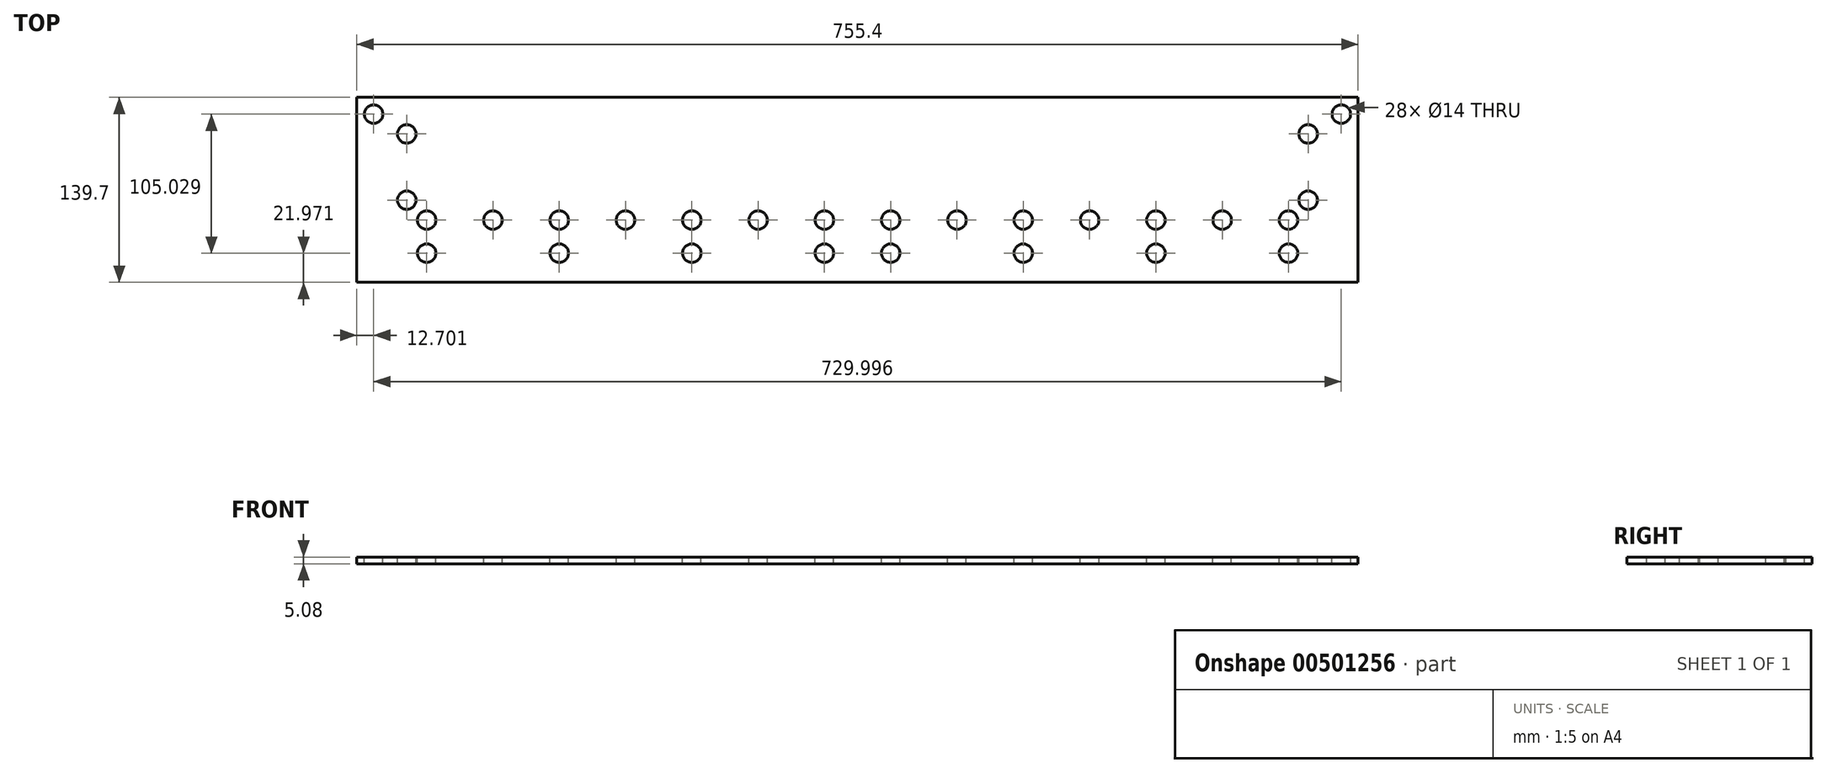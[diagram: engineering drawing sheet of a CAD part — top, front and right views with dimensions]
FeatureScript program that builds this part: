
annotation { "Feature Type Name" : "Feature", "Feature Type Description" : "" }
export const myFeature = defineFeature(function(context is Context, id is Id, definition is map)
    precondition{}
    {
        {
            var Q0;
            Q0=qCreatedBy(makeId("Top.planeOp"),FACE);
            var sketch = newSketch(context, id + "F0", { "sketchPlane" : qUnion([Q0])});
            skLineSegment(sketch, "E0.bottom", {"start": v(1.3, 0) * mm, "end": v(756.69, 0) * mm});
            skLineSegment(sketch, "E0.top", {"start": v(1.3, 139.7) * mm, "end": v(756.69, 139.7) * mm});
            skLineSegment(sketch, "E0.left", {"start": v(1.3, 0) * mm, "end": v(1.3, 139.7) * mm});
            skLineSegment(sketch, "E0.right", {"start": v(756.69, 0) * mm, "end": v(756.69, 139.7) * mm});
            skSolve(sketch);
        }
        {
            var Q0;
            Q0 = qSketchRegion(id + "F0", true);
            extrude(context, id + "F1", {"entities" : qUnion([Q0]), "depth" : 5.08 * mm, "offsetDistance" : 25.4 * mm});
        }
        {
            var Q0;
            Q0=makeQuery(id+"F1.opExtrude","CAP_FACE",FACE,{"disambiguationData":[OSD([sQuery(id+"F0.wireOp",EDGE,"E0.bottom"),sQuery(id+"F0.wireOp",EDGE,"E0.top"),sQuery(id+"F0.wireOp",EDGE,"E0.left"),sQuery(id+"F0.wireOp",EDGE,"E0.right")])],"isStart":false});
            var sketch = newSketch(context, id + "F2", { "sketchPlane" : qUnion([Q0])});
            skLineSegment(sketch, "E1", {"start": v(1.3, 139.7) * mm, "end": v(14, 139.7) * mm});
            skLineSegment(sketch, "E2", {"start": v(14, 139.7) * mm, "end": v(14, 127) * mm});
            skCircle(sketch, "E3", {"center": v(14, 127) * mm, "radius": 3.94 * mm});
            skLineSegment(sketch, "E4", {"start": v(14, 127) * mm, "end": v(38.98, 127) * mm});
            skLineSegment(sketch, "E5", {"start": v(38.98, 127) * mm, "end": v(38.98, 111.99) * mm});
            skCircle(sketch, "E6", {"center": v(38.98, 111.99) * mm, "radius": 3.94 * mm});
            skLineSegment(sketch, "E7", {"start": v(38.98, 111.99) * mm, "end": v(38.98, 61.98) * mm});
            skCircle(sketch, "E8", {"center": v(38.98, 61.98) * mm, "radius": 3.94 * mm});
            skLineSegment(sketch, "E9", {"start": v(38.98, 61.98) * mm, "end": v(54, 61.98) * mm});
            skLineSegment(sketch, "E10", {"start": v(54, 61.98) * mm, "end": v(54, 46.96) * mm});
            skCircle(sketch, "E11", {"center": v(54, 46.96) * mm, "radius": 3.94 * mm});
            skLineSegment(sketch, "E12", {"start": v(54, 46.96) * mm, "end": v(54, 21.97) * mm});
            skCircle(sketch, "E13", {"center": v(54, 21.97) * mm, "radius": 3.94 * mm});
            skLineSegment(sketch, "E14", {"start": v(378.99, 139.7) * mm, "end": v(378.99, 187.38) * mm});
            skCircle(sketch, "E15.1.0.0", {"center": v(104, 46.96) * mm, "radius": 3.94 * mm});
            skCircle(sketch, "E15.2.0.0", {"center": v(154.02, 46.96) * mm, "radius": 3.94 * mm});
            skCircle(sketch, "E15.3.0.0", {"center": v(204.03, 46.96) * mm, "radius": 3.94 * mm});
            skCircle(sketch, "E15.4.0.0", {"center": v(254.05, 46.96) * mm, "radius": 3.94 * mm});
            skCircle(sketch, "E15.5.0.0", {"center": v(304.06, 46.96) * mm, "radius": 3.94 * mm});
            skCircle(sketch, "E15.6.0.0", {"center": v(354.07, 46.96) * mm, "radius": 3.94 * mm});
            skLineSegment(sketch, "E15.direction1", {"start": v(54, 46.96) * mm, "end": v(104, 46.96) * mm, "construction": true});
            skCircle(sketch, "E16.0.7.0", {"center": v(404.08, 46.96) * mm, "radius": 3.94 * mm});
            skCircle(sketch, "E16.0.8.0", {"center": v(454.1, 46.96) * mm, "radius": 3.94 * mm});
            skCircle(sketch, "E16.0.9.0", {"center": v(504.1, 46.96) * mm, "radius": 3.94 * mm});
            skCircle(sketch, "E16.0.10.0", {"center": v(554.12, 46.96) * mm, "radius": 3.94 * mm});
            skCircle(sketch, "E16.0.11.0", {"center": v(604.13, 46.96) * mm, "radius": 3.94 * mm});
            skCircle(sketch, "E16.0.12.0", {"center": v(654.15, 46.96) * mm, "radius": 3.94 * mm});
            skCircle(sketch, "E16.0.13.0", {"center": v(704.16, 46.96) * mm, "radius": 3.94 * mm});
            skCircle(sketch, "E17.1.0.0", {"center": v(154.02, 21.97) * mm, "radius": 3.94 * mm});
            skCircle(sketch, "E17.2.0.0", {"center": v(254.05, 21.97) * mm, "radius": 3.94 * mm});
            skCircle(sketch, "E17.3.0.0", {"center": v(354.07, 21.97) * mm, "radius": 3.94 * mm});
            skLineSegment(sketch, "E17.direction1", {"start": v(54, 21.97) * mm, "end": v(154.02, 21.97) * mm, "construction": true});
            skCircle(sketch, "E18.MirrorC", {"center": v(743.99, 127) * mm, "radius": 3.94 * mm});
            skCircle(sketch, "E19.MirrorC", {"center": v(719, 111.99) * mm, "radius": 3.94 * mm});
            skCircle(sketch, "E20.MirrorC", {"center": v(719, 61.98) * mm, "radius": 3.94 * mm});
            skLineSegment(sketch, "E21", {"start": v(354.07, 21.97) * mm, "end": v(404.08, 21.97) * mm});
            skCircle(sketch, "E22", {"center": v(404.08, 21.97) * mm, "radius": 3.94 * mm});
            skCircle(sketch, "E23.1.0.0", {"center": v(504.1, 21.97) * mm, "radius": 3.94 * mm});
            skCircle(sketch, "E23.2.0.0", {"center": v(604.13, 21.97) * mm, "radius": 3.94 * mm});
            skCircle(sketch, "E23.3.0.0", {"center": v(704.16, 21.97) * mm, "radius": 3.94 * mm});
            skLineSegment(sketch, "E23.direction1", {"start": v(404.08, 21.97) * mm, "end": v(504.1, 21.97) * mm, "construction": true});
            skSolve(sketch);
        }
        {
            var Q0;
            Q0=sQuery(id+"F2.wireOp",VERTEX,"E3.center");
            var Q1;
            Q1=sQuery(id+"F2.wireOp",VERTEX,"E7.start");
            var Q2;
            Q2=sQuery(id+"F2.wireOp",VERTEX,"E9.start");
            var Q3;
            Q3=sQuery(id+"F2.wireOp",VERTEX,"E11.center");
            var Q4;
            Q4=sQuery(id+"F2.wireOp",VERTEX,"E17.direction1.start");
            var Q5;
            Q5=sQuery(id+"F2.wireOp",VERTEX,"E15.direction1.end");
            var Q6;
            Q6=sQuery(id+"F2.wireOp",VERTEX,"E17.1.0.0.center");
            var Q7;
            Q7=sQuery(id+"F2.wireOp",VERTEX,"E15.2.0.0.center");
            var Q8;
            Q8=sQuery(id+"F2.wireOp",VERTEX,"E15.3.0.0.center");
            var Q9;
            Q9=sQuery(id+"F2.wireOp",VERTEX,"E17.2.0.0.center");
            var Q10;
            Q10=sQuery(id+"F2.wireOp",VERTEX,"E15.4.0.0.center");
            var Q11;
            Q11=sQuery(id+"F2.wireOp",VERTEX,"E15.5.0.0.center");
            var Q12;
            Q12=sQuery(id+"F2.wireOp",VERTEX,"E15.6.0.0.center");
            var Q13;
            Q13=sQuery(id+"F2.wireOp",VERTEX,"E21.start");
            var Q14;
            Q14=sQuery(id+"F2.wireOp",VERTEX,"E22.center");
            var Q15;
            Q15=sQuery(id+"F2.wireOp",VERTEX,"E16.0.7.0.center");
            var Q16;
            Q16=sQuery(id+"F2.wireOp",VERTEX,"E16.0.8.0.center");
            var Q17;
            Q17=sQuery(id+"F2.wireOp",VERTEX,"E23.1.0.0.center");
            var Q18;
            Q18=sQuery(id+"F2.wireOp",VERTEX,"E16.0.9.0.center");
            var Q19;
            Q19=sQuery(id+"F2.wireOp",VERTEX,"E16.0.10.0.center");
            var Q20;
            Q20=sQuery(id+"F2.wireOp",VERTEX,"E16.0.11.0.center");
            var Q21;
            Q21=sQuery(id+"F2.wireOp",VERTEX,"E23.2.0.0.center");
            var Q22;
            Q22=sQuery(id+"F2.wireOp",VERTEX,"E18.MirrorC.center");
            var Q23;
            Q23=sQuery(id+"F2.wireOp",VERTEX,"E19.MirrorC.center");
            var Q24;
            Q24=sQuery(id+"F2.wireOp",VERTEX,"E20.MirrorC.center");
            var Q25;
            Q25=sQuery(id+"F2.wireOp",VERTEX,"E16.0.13.0.center");
            var Q26;
            Q26=sQuery(id+"F2.wireOp",VERTEX,"E23.3.0.0.center");
            var Q27;
            Q27=sQuery(id+"F2.wireOp",VERTEX,"E16.0.12.0.center");
            var Q28;
            Q28=makeQuery(id+"F1.opExtrude","SWEPT_BODY",BODY,{"disambiguationData":[OSD([sQuery(id+"F0.wireOp",EDGE,"E0.bottom"),sQuery(id+"F0.wireOp",EDGE,"E0.top"),sQuery(id+"F0.wireOp",EDGE,"E0.left"),sQuery(id+"F0.wireOp",EDGE,"E0.right")])]});
            hole(context, id + "F3", {"style" : HoleStyle.C_BORE, "endStyle" : HoleEndStyle.THROUGH, "holeDiameter" : 8.5 * mm, "cBoreDiameter" : 14 * mm, "cBoreDepth" : 8.5 * mm, "isTappedThrough" : true, "tappedDepth" : 12.7 * mm, "tapClearance" : 3, "locations" : qUnion([Q0, Q1, Q2, Q3, Q4, Q5, Q6, Q7, Q8, Q9, Q10, Q11, Q12, Q13, Q14, Q15, Q16, Q17, Q18, Q19, Q20, Q21, Q22, Q23, Q24, Q25, Q26, Q27]), "scope" : qUnion([Q28])});
        }
    });
